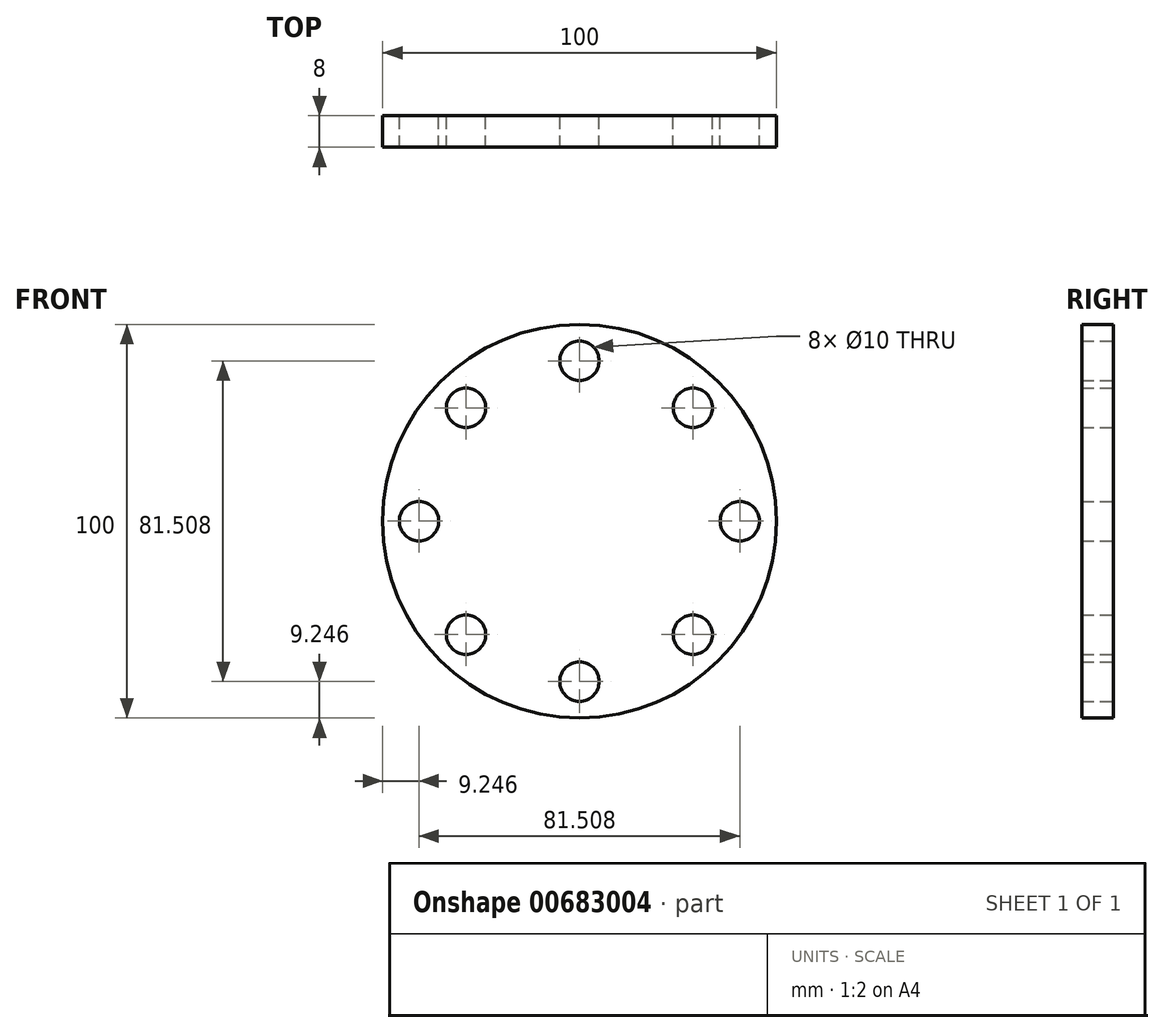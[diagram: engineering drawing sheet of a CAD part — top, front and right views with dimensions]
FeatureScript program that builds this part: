
annotation { "Feature Type Name" : "Feature", "Feature Type Description" : "" }
export const myFeature = defineFeature(function(context is Context, id is Id, definition is map)
    precondition{}
    {
        {
            var Q0;
            Q0=qCreatedBy(makeId("Front.planeOp"),FACE);
            var sketch = newSketch(context, id + "F0", { "sketchPlane" : qUnion([Q0])});
            skCircle(sketch, "E0", {"center": v(0, 0) * mm, "radius": 50 * mm});
            skCircle(sketch, "E1", {"center": v(0, 40.75) * mm, "radius": 5 * mm});
            skCircle(sketch, "E2.1.0", {"center": v(-28.82, 28.82) * mm, "radius": 5 * mm});
            skCircle(sketch, "E2.2.0", {"center": v(-40.75, 0) * mm, "radius": 5 * mm});
            skCircle(sketch, "E2.3.0", {"center": v(-28.82, -28.82) * mm, "radius": 5 * mm});
            skCircle(sketch, "E2.4.0", {"center": v(0, -40.75) * mm, "radius": 5 * mm});
            skCircle(sketch, "E2.5.0", {"center": v(28.82, -28.82) * mm, "radius": 5 * mm});
            skCircle(sketch, "E2.6.0", {"center": v(40.75, 0) * mm, "radius": 5 * mm});
            skCircle(sketch, "E2.7.0", {"center": v(28.82, 28.82) * mm, "radius": 5 * mm});
            skSolve(sketch);
        }
        {
            var Q0;
            Q0 = qSketchRegion(id + "F0", true);
            extrude(context, id + "F1", {"entities" : qUnion([Q0]), "depth" : 8 * mm, "offsetDistance" : 25 * mm});
        }
    });
